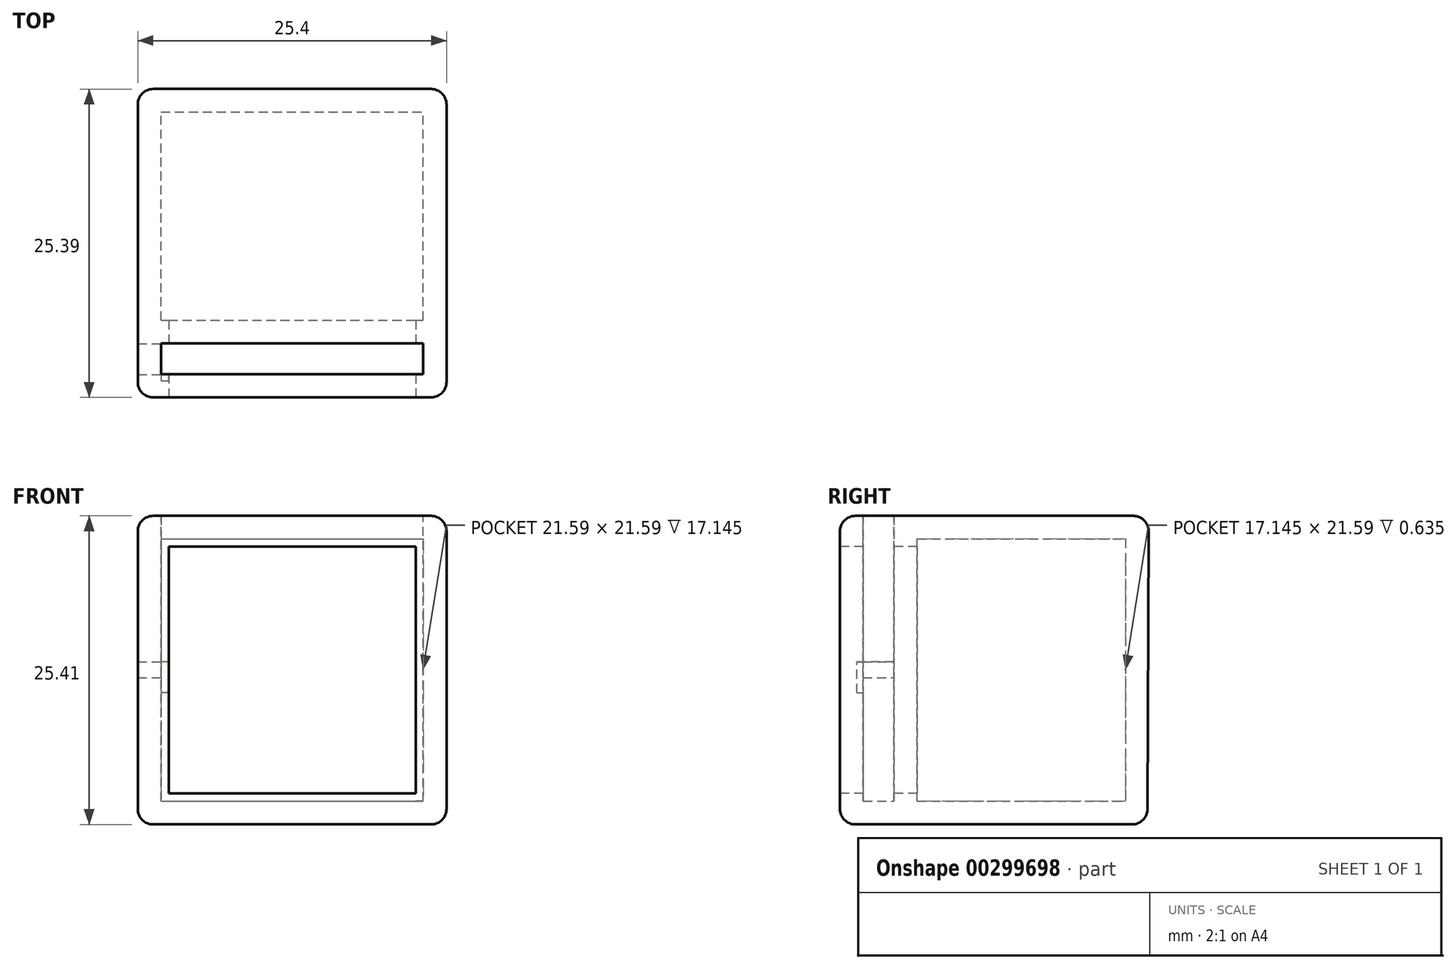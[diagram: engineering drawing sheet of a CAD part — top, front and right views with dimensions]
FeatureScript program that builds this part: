
annotation { "Feature Type Name" : "Feature", "Feature Type Description" : "" }
export const myFeature = defineFeature(function(context is Context, id is Id, definition is map)
    precondition{}
    {
        {
            var Q0;
            Q0=qCreatedBy(makeId("Front.planeOp"),FACE);
            var sketch = newSketch(context, id + "F0", { "sketchPlane" : qUnion([Q0])});
            skLineSegment(sketch, "E0.top", {"start": v(-12.7, -1.9) * mm, "end": v(12.7, -1.9) * mm});
            skPoint(sketch, "E0.middle", {"position": v(0, 0) * mm});
            skLineSegment(sketch, "E1", {"start": v(10.8, 21.6) * mm, "end": v(10.8, 0) * mm});
            skLineSegment(sketch, "E2", {"start": v(-10.8, 21.6) * mm, "end": v(-10.8, 0) * mm});
            skLineSegment(sketch, "E3.top", {"start": v(-12.7, 23.5) * mm, "end": v(12.7, 23.5) * mm});
            skLineSegment(sketch, "E4", {"start": v(-10.8, 21.6) * mm, "end": v(10.8, 21.6) * mm});
            skLineSegment(sketch, "E5", {"start": v(-10.8, 0) * mm, "end": v(10.8, 0) * mm});
            skLineSegment(sketch, "E6", {"start": v(-12.7, -1.9) * mm, "end": v(-12.7, 23.5) * mm});
            skLineSegment(sketch, "E7", {"start": v(12.7, -1.9) * mm, "end": v(12.7, 23.5) * mm});
            skSolve(sketch);
        }
        {
            var Q0;
            Q0=qCreatedBy(makeId("Right.planeOp"),FACE);
            var sketch = newSketch(context, id + "F1", { "sketchPlane" : qUnion([Q0])});
            skLineSegment(sketch, "E8.bottom", {"start": v(8.57, 23.5) * mm, "end": v(10.48, 23.5) * mm});
            skLineSegment(sketch, "E8.left", {"start": v(8.57, 23.5) * mm, "end": v(8.57, 23.5) * mm});
            skLineSegment(sketch, "E8.right", {"start": v(10.48, 23.5) * mm, "end": v(10.36, -1.9) * mm});
            skLineSegment(sketch, "E9", {"start": v(8.57, -1.9) * mm, "end": v(10.36, -1.9) * mm});
            skLineSegment(sketch, "E10.bottom", {"start": v(-8.57, 0.63) * mm, "end": v(-10.48, 0.63) * mm});
            skLineSegment(sketch, "E10.left", {"start": v(-8.57, 0.63) * mm, "end": v(-8.57, -1.9) * mm});
            skLineSegment(sketch, "E11.right", {"start": v(-14.92, 0.63) * mm, "end": v(-14.92, -1.9) * mm});
            skLineSegment(sketch, "E12", {"start": v(-14.92, 20.96) * mm, "end": v(-14.92, 23.5) * mm});
            skLineSegment(sketch, "E13", {"start": v(-8.57, 23.5) * mm, "end": v(-8.57, 20.96) * mm});
            skLineSegment(sketch, "E14", {"start": v(-8.57, 20.96) * mm, "end": v(-10.48, 20.95) * mm});
            skLineSegment(sketch, "E15", {"start": v(-10.48, 20.95) * mm, "end": v(-10.48, 23.5) * mm});
            skLineSegment(sketch, "E16", {"start": v(-13.02, 23.5) * mm, "end": v(-13.02, 20.96) * mm});
            skLineSegment(sketch, "E17", {"start": v(-13.02, 20.96) * mm, "end": v(-14.92, 20.96) * mm});
            skLineSegment(sketch, "E18", {"start": v(-13.02, 23.5) * mm, "end": v(-14.92, 23.5) * mm});
            skLineSegment(sketch, "E19", {"start": v(-8.57, 23.5) * mm, "end": v(-10.48, 23.5) * mm});
            skLineSegment(sketch, "E20", {"start": v(-14.92, -1.9) * mm, "end": v(-8.57, -1.9) * mm});
            skLineSegment(sketch, "E21", {"start": v(-10.48, 0.63) * mm, "end": v(-10.48, 0) * mm});
            skLineSegment(sketch, "E22", {"start": v(-10.48, 0) * mm, "end": v(-13.02, 0) * mm});
            skLineSegment(sketch, "E23", {"start": v(-13.02, 0) * mm, "end": v(-13.02, 0.63) * mm});
            skLineSegment(sketch, "E24", {"start": v(-13.02, 0.63) * mm, "end": v(-14.92, 0.63) * mm});
            skLineSegment(sketch, "E25", {"start": v(8.57, -1.9) * mm, "end": v(8.57, 23.5) * mm});
            skSolve(sketch);
        }
        {
            var Q0;
            Q0=makeQuery(id+"F0.imprint","IMPRINT",FACE,{"disambiguationData":[TD([[makeQuery(id+"F0.imprint","IMPRINT",EDGE,{"derivedFrom":sQuery(id+"F0.wireOp",EDGE,"E0.top")}),1.0]])]});
            extrude(context, id + "F2", {"entities" : qUnion([Q0]), "endBound" : BoundingType.SYMMETRIC, "depth" : 17.14 * mm});
        }
        {
            var Q0;
            Q0 = qSketchRegion(id + "F1", true);
            extrude(context, id + "F3", {"entities" : qUnion([Q0]), "endBound" : BoundingType.SYMMETRIC, "depth" : 25.4 * mm});
        }
        {
            var Q0;
            Q0=qCreatedBy(makeId("Top.planeOp"),FACE);
            var sketch = newSketch(context, id + "F4", { "sketchPlane" : qUnion([Q0])});
            skLineSegment(sketch, "E26", {"start": v(-12.7, -8.57) * mm, "end": v(-12.7, -14.92) * mm});
            skLineSegment(sketch, "E27", {"start": v(-12.7, -14.92) * mm, "end": v(-10.16, -14.92) * mm});
            skLineSegment(sketch, "E28", {"start": v(-10.16, -14.92) * mm, "end": v(-10.16, -13.02) * mm});
            skLineSegment(sketch, "E29", {"start": v(-10.16, -13.02) * mm, "end": v(-10.8, -13.02) * mm});
            skLineSegment(sketch, "E30", {"start": v(-10.8, -13.02) * mm, "end": v(-10.8, -10.48) * mm});
            skLineSegment(sketch, "E31", {"start": v(-10.8, -10.48) * mm, "end": v(-10.16, -10.48) * mm});
            skLineSegment(sketch, "E32", {"start": v(-10.16, -10.48) * mm, "end": v(-10.16, -8.57) * mm});
            skLineSegment(sketch, "E33", {"start": v(-10.16, -8.57) * mm, "end": v(-12.7, -8.57) * mm});
            skLineSegment(sketch, "E34.MirrorCS", {"start": v(10.16, -8.57) * mm, "end": v(12.7, -8.57) * mm});
            skLineSegment(sketch, "E35.MirrorCS", {"start": v(10.16, -10.48) * mm, "end": v(10.16, -8.57) * mm});
            skLineSegment(sketch, "E36.MirrorCS", {"start": v(10.8, -10.48) * mm, "end": v(10.16, -10.48) * mm});
            skLineSegment(sketch, "E37.MirrorCS", {"start": v(10.8, -13.02) * mm, "end": v(10.8, -10.48) * mm});
            skLineSegment(sketch, "E38.MirrorCS", {"start": v(10.16, -13.02) * mm, "end": v(10.8, -13.02) * mm});
            skLineSegment(sketch, "E39.MirrorCS", {"start": v(10.16, -14.92) * mm, "end": v(10.16, -13.02) * mm});
            skLineSegment(sketch, "E40.MirrorCS", {"start": v(12.7, -8.57) * mm, "end": v(12.7, -14.92) * mm});
            skLineSegment(sketch, "E41.MirrorCS", {"start": v(12.7, -14.92) * mm, "end": v(10.16, -14.92) * mm});
            skSolve(sketch);
        }
        {
            var Q0;
            Q0=makeQuery(id+"F4.imprint","IMPRINT",FACE,{"disambiguationData":[TD([[makeQuery(id+"F4.imprint","IMPRINT",EDGE,{"derivedFrom":sQuery(id+"F4.wireOp",EDGE,"E26")}),1.0]])]});
            var Q1;
            Q1=makeQuery(id+"F4.imprint","IMPRINT",FACE,{"disambiguationData":[TD([[makeQuery(id+"F4.imprint","IMPRINT",EDGE,{"derivedFrom":sQuery(id+"F4.wireOp",EDGE,"E34.MirrorCS")}),-1.0]])]});
            extrude(context, id + "F5", {"entities" : qUnion([Q0, Q1]), "depth" : 23.5 * mm});
        }
        {
            var Q0;
            Q0=makeQuery(id+"F5.opExtrude","SWEPT_BODY",BODY,{"disambiguationData":[OSD([sQuery(id+"F4.wireOp",EDGE,"E34.MirrorCS"),sQuery(id+"F4.wireOp",EDGE,"E35.MirrorCS"),sQuery(id+"F4.wireOp",EDGE,"E36.MirrorCS"),sQuery(id+"F4.wireOp",EDGE,"E37.MirrorCS"),sQuery(id+"F4.wireOp",EDGE,"E38.MirrorCS"),sQuery(id+"F4.wireOp",EDGE,"E39.MirrorCS"),sQuery(id+"F4.wireOp",EDGE,"E40.MirrorCS"),sQuery(id+"F4.wireOp",EDGE,"E41.MirrorCS")])]});
            var Q1;
            Q1=makeQuery(id+"F5.opExtrude","SWEPT_BODY",BODY,{"disambiguationData":[OSD([sQuery(id+"F4.wireOp",EDGE,"E26"),sQuery(id+"F4.wireOp",EDGE,"E27"),sQuery(id+"F4.wireOp",EDGE,"E28"),sQuery(id+"F4.wireOp",EDGE,"E29"),sQuery(id+"F4.wireOp",EDGE,"E30"),sQuery(id+"F4.wireOp",EDGE,"E31"),sQuery(id+"F4.wireOp",EDGE,"E32"),sQuery(id+"F4.wireOp",EDGE,"E33")])]});
            var Q2;
            Q2=makeQuery(id+"F3.opExtrude","SWEPT_BODY",BODY,{"disambiguationData":[OSD([sQuery(id+"F1.wireOp",EDGE,"E13"),sQuery(id+"F1.wireOp",EDGE,"E14"),sQuery(id+"F1.wireOp",EDGE,"E15"),sQuery(id+"F1.wireOp",EDGE,"E19")])]});
            var Q3;
            Q3=makeQuery(id+"F3.opExtrude","SWEPT_BODY",BODY,{"disambiguationData":[OSD([sQuery(id+"F1.wireOp",EDGE,"E12"),sQuery(id+"F1.wireOp",EDGE,"E16"),sQuery(id+"F1.wireOp",EDGE,"E17"),sQuery(id+"F1.wireOp",EDGE,"E18")])]});
            var Q4;
            Q4=makeQuery(id+"F3.opExtrude","SWEPT_BODY",BODY,{"disambiguationData":[OSD([sQuery(id+"F1.wireOp",EDGE,"E10.bottom"),sQuery(id+"F1.wireOp",EDGE,"E10.left"),sQuery(id+"F1.wireOp",EDGE,"E11.right"),sQuery(id+"F1.wireOp",EDGE,"E20"),sQuery(id+"F1.wireOp",EDGE,"E21"),sQuery(id+"F1.wireOp",EDGE,"E22"),sQuery(id+"F1.wireOp",EDGE,"E23"),sQuery(id+"F1.wireOp",EDGE,"E24")])]});
            var Q5;
            Q5=makeQuery(id+"F3.opExtrude","SWEPT_BODY",BODY,{"disambiguationData":[OSD([sQuery(id+"F1.wireOp",EDGE,"E8.bottom"),sQuery(id+"F1.wireOp",EDGE,"E8.right"),sQuery(id+"F1.wireOp",EDGE,"E9"),sQuery(id+"F1.wireOp",EDGE,"E25")])]});
            var Q6;
            Q6=makeQuery(id+"F2.opExtrude","SWEPT_BODY",BODY,{"disambiguationData":[OSD([sQuery(id+"F0.wireOp",EDGE,"E0.top"),sQuery(id+"F0.wireOp",EDGE,"E1"),sQuery(id+"F0.wireOp",EDGE,"E2"),sQuery(id+"F0.wireOp",EDGE,"E3.top"),sQuery(id+"F0.wireOp",EDGE,"E4"),sQuery(id+"F0.wireOp",EDGE,"E5"),sQuery(id+"F0.wireOp",EDGE,"E6"),sQuery(id+"F0.wireOp",EDGE,"E7")])]});
            booleanBodies(context, id + "F6", {"operationType" : BooleanOperationType.UNION, "tools" : qUnion([Q0, Q1, Q2, Q3, Q4, Q5, Q6])});
        }
        {
            var Q0;
            Q0=qCreatedBy(makeId("Right.planeOp"),FACE);
            var sketch = newSketch(context, id + "F7", { "sketchPlane" : qUnion([Q0])});
            skLineSegment(sketch, "E42.bottom", {"start": v(-10.5, 10.16) * mm, "end": v(-13.03, 10.16) * mm});
            skLineSegment(sketch, "E42.top", {"start": v(-10.5, 11.47) * mm, "end": v(-13.03, 11.47) * mm});
            skLineSegment(sketch, "E42.left", {"start": v(-10.5, 10.16) * mm, "end": v(-10.5, 11.47) * mm});
            skLineSegment(sketch, "E42.right", {"start": v(-13.03, 10.16) * mm, "end": v(-13.03, 11.47) * mm});
            skLineSegment(sketch, "E43", {"start": v(-13.03, 11.47) * mm, "end": v(-13.54, 11.47) * mm});
            skLineSegment(sketch, "E44", {"start": v(-13.54, 11.47) * mm, "end": v(-13.54, 8.93) * mm});
            skLineSegment(sketch, "E45", {"start": v(-12.65, 10.16) * mm, "end": v(-12.65, 8.93) * mm});
            skLineSegment(sketch, "E46", {"start": v(-12.65, 8.93) * mm, "end": v(-13.54, 8.93) * mm});
            skSolve(sketch);
        }
        {
            var Q0;
            Q0=makeQuery(id+"F7.imprint","IMPRINT",FACE,{"disambiguationData":[TD([[makeQuery(id+"F7.imprint","IMPRINT",EDGE,{"derivedFrom":sQuery(id+"F7.wireOp",EDGE,"E42.bottom")}),-1.0]])]});
            extrude(context, id + "F8", {"entities" : qUnion([Q0]), "operationType" : NewBodyOperationType.REMOVE, "oppositeDirection" : true, "depth" : 12.7 * mm});
        }
        {
            var Q0;
            Q0=makeQuery(id+"F7.imprint","IMPRINT",FACE,{"disambiguationData":[TD([[makeQuery(id+"F7.imprint","IMPRINT",EDGE,{"derivedFrom":sQuery(id+"F7.wireOp",EDGE,"E42.right")}),1.0]])]});
            extrude(context, id + "F9", {"entities" : qUnion([Q0]), "operationType" : NewBodyOperationType.REMOVE, "oppositeDirection" : true, "depth" : 10.8 * mm});
        }
        {
            var Q0;
            Q0=makeQuery(id+"F2.opExtrude","SWEPT_EDGE",EDGE,{"disambiguationData":[OSD([sQuery(id+"F0.wireOp",EDGE,"E3.top"),sQuery(id+"F0.wireOp",EDGE,"E7")])]});
            var Q1;
            Q1=makeQuery(id+"F3.opExtrude","CAP_EDGE",EDGE,{"disambiguationData":[OSD([sQuery(id+"F1.wireOp",EDGE,"E8.bottom")])],"isStart":false});
            var Q2;
            {var subQ0=sQuery(id+"F4.wireOp",EDGE,"E40.MirrorCS");Q2=makeQuery(id+"F6.opBoolean","SPLIT",EDGE,{"disambiguationData":[TD([makeQuery(id+"F2.opExtrude","SWEPT_FACE",FACE,{"disambiguationData":[OSD([sQuery(id+"F0.wireOp",EDGE,"E3.top")])]}),makeQuery(id+"F2.opExtrude","SWEPT_FACE",FACE,{"disambiguationData":[OSD([sQuery(id+"F0.wireOp",EDGE,"E7")])]}),makeQuery(id+"F3.opExtrude","CAP_FACE",FACE,{"disambiguationData":[OSD([sQuery(id+"F1.wireOp",EDGE,"E8.bottom"),sQuery(id+"F1.wireOp",EDGE,"E8.right"),sQuery(id+"F1.wireOp",EDGE,"E9"),sQuery(id+"F1.wireOp",EDGE,"E25")])],"isStart":false}),makeQuery(id+"F3.opExtrude","CAP_FACE",FACE,{"disambiguationData":[OSD([sQuery(id+"F1.wireOp",EDGE,"E10.bottom"),sQuery(id+"F1.wireOp",EDGE,"E10.left"),sQuery(id+"F1.wireOp",EDGE,"E11.right"),sQuery(id+"F1.wireOp",EDGE,"E20"),sQuery(id+"F1.wireOp",EDGE,"E21"),sQuery(id+"F1.wireOp",EDGE,"E22"),sQuery(id+"F1.wireOp",EDGE,"E23"),sQuery(id+"F1.wireOp",EDGE,"E24")])],"isStart":false}),makeQuery(id+"F3.opExtrude","CAP_FACE",FACE,{"disambiguationData":[OSD([sQuery(id+"F1.wireOp",EDGE,"E13"),sQuery(id+"F1.wireOp",EDGE,"E14"),sQuery(id+"F1.wireOp",EDGE,"E15"),sQuery(id+"F1.wireOp",EDGE,"E19")])],"isStart":false}),makeQuery(id+"F3.opExtrude","SWEPT_FACE",FACE,{"disambiguationData":[OSD([sQuery(id+"F1.wireOp",EDGE,"E18")])]}),makeQuery(id+"F5.opExtrude","CAP_FACE",FACE,{"disambiguationData":[OSD([sQuery(id+"F4.wireOp",EDGE,"E26"),sQuery(id+"F4.wireOp",EDGE,"E27"),sQuery(id+"F4.wireOp",EDGE,"E28"),sQuery(id+"F4.wireOp",EDGE,"E29"),sQuery(id+"F4.wireOp",EDGE,"E30"),sQuery(id+"F4.wireOp",EDGE,"E31"),sQuery(id+"F4.wireOp",EDGE,"E32"),sQuery(id+"F4.wireOp",EDGE,"E33")])],"isStart":false}),makeQuery(id+"F5.opExtrude","CAP_FACE",FACE,{"disambiguationData":[OSD([sQuery(id+"F4.wireOp",EDGE,"E34.MirrorCS"),sQuery(id+"F4.wireOp",EDGE,"E35.MirrorCS"),sQuery(id+"F4.wireOp",EDGE,"E36.MirrorCS"),sQuery(id+"F4.wireOp",EDGE,"E37.MirrorCS"),sQuery(id+"F4.wireOp",EDGE,"E38.MirrorCS"),sQuery(id+"F4.wireOp",EDGE,"E39.MirrorCS"),subQ0,sQuery(id+"F4.wireOp",EDGE,"E41.MirrorCS")])],"isStart":false}),makeQuery(id+"F5.opExtrude","SWEPT_FACE",FACE,{"disambiguationData":[OSD([subQ0])]})])],"derivedFrom":makeQuery(id+"F5.opExtrude","CAP_EDGE",EDGE,{"disambiguationData":[OSD([subQ0])],"isStart":false})});}
            var Q3;
            {var subQ0=sQuery(id+"F4.wireOp",EDGE,"E41.MirrorCS");var subQ1=sQuery(id+"F4.wireOp",EDGE,"E40.MirrorCS");Q3=makeQuery(id+"F6.opBoolean","SPLIT",EDGE,{"disambiguationData":[TD([makeQuery(id+"F2.opExtrude","SWEPT_FACE",FACE,{"disambiguationData":[OSD([sQuery(id+"F0.wireOp",EDGE,"E7")])]}),makeQuery(id+"F3.opExtrude","CAP_FACE",FACE,{"disambiguationData":[OSD([sQuery(id+"F1.wireOp",EDGE,"E8.bottom"),sQuery(id+"F1.wireOp",EDGE,"E8.right"),sQuery(id+"F1.wireOp",EDGE,"E9"),sQuery(id+"F1.wireOp",EDGE,"E25")])],"isStart":false}),makeQuery(id+"F3.opExtrude","CAP_FACE",FACE,{"disambiguationData":[OSD([sQuery(id+"F1.wireOp",EDGE,"E10.bottom"),sQuery(id+"F1.wireOp",EDGE,"E10.left"),sQuery(id+"F1.wireOp",EDGE,"E11.right"),sQuery(id+"F1.wireOp",EDGE,"E20"),sQuery(id+"F1.wireOp",EDGE,"E21"),sQuery(id+"F1.wireOp",EDGE,"E22"),sQuery(id+"F1.wireOp",EDGE,"E23"),sQuery(id+"F1.wireOp",EDGE,"E24")])],"isStart":false}),makeQuery(id+"F3.opExtrude","CAP_FACE",FACE,{"disambiguationData":[OSD([sQuery(id+"F1.wireOp",EDGE,"E13"),sQuery(id+"F1.wireOp",EDGE,"E14"),sQuery(id+"F1.wireOp",EDGE,"E15"),sQuery(id+"F1.wireOp",EDGE,"E19")])],"isStart":false}),makeQuery(id+"F3.opExtrude","SWEPT_FACE",FACE,{"disambiguationData":[OSD([sQuery(id+"F1.wireOp",EDGE,"E18")])]}),makeQuery(id+"F5.opExtrude","CAP_FACE",FACE,{"disambiguationData":[OSD([sQuery(id+"F4.wireOp",EDGE,"E26"),sQuery(id+"F4.wireOp",EDGE,"E27"),sQuery(id+"F4.wireOp",EDGE,"E28"),sQuery(id+"F4.wireOp",EDGE,"E29"),sQuery(id+"F4.wireOp",EDGE,"E30"),sQuery(id+"F4.wireOp",EDGE,"E31"),sQuery(id+"F4.wireOp",EDGE,"E32"),sQuery(id+"F4.wireOp",EDGE,"E33")])],"isStart":false}),makeQuery(id+"F5.opExtrude","CAP_FACE",FACE,{"disambiguationData":[OSD([sQuery(id+"F4.wireOp",EDGE,"E34.MirrorCS"),sQuery(id+"F4.wireOp",EDGE,"E35.MirrorCS"),sQuery(id+"F4.wireOp",EDGE,"E36.MirrorCS"),sQuery(id+"F4.wireOp",EDGE,"E37.MirrorCS"),sQuery(id+"F4.wireOp",EDGE,"E38.MirrorCS"),sQuery(id+"F4.wireOp",EDGE,"E39.MirrorCS"),subQ1,subQ0])],"isStart":false}),makeQuery(id+"F5.opExtrude","SWEPT_FACE",FACE,{"disambiguationData":[OSD([subQ1])]}),makeQuery(id+"F5.opExtrude","SWEPT_FACE",FACE,{"disambiguationData":[OSD([subQ0])]})])],"derivedFrom":makeQuery(id+"F5.opExtrude","CAP_EDGE",EDGE,{"disambiguationData":[OSD([subQ1])],"isStart":false})});}
            var Q4;
            {var subQ0=sQuery(id+"F4.wireOp",EDGE,"E40.MirrorCS");Q4=makeQuery(id+"F6.opBoolean","SPLIT",EDGE,{"disambiguationData":[TD([makeQuery(id+"F2.opExtrude","SWEPT_FACE",FACE,{"disambiguationData":[OSD([sQuery(id+"F0.wireOp",EDGE,"E7")])]}),makeQuery(id+"F3.opExtrude","CAP_FACE",FACE,{"disambiguationData":[OSD([sQuery(id+"F1.wireOp",EDGE,"E8.bottom"),sQuery(id+"F1.wireOp",EDGE,"E8.right"),sQuery(id+"F1.wireOp",EDGE,"E9"),sQuery(id+"F1.wireOp",EDGE,"E25")])],"isStart":false}),makeQuery(id+"F3.opExtrude","CAP_FACE",FACE,{"disambiguationData":[OSD([sQuery(id+"F1.wireOp",EDGE,"E10.bottom"),sQuery(id+"F1.wireOp",EDGE,"E10.left"),sQuery(id+"F1.wireOp",EDGE,"E11.right"),sQuery(id+"F1.wireOp",EDGE,"E20"),sQuery(id+"F1.wireOp",EDGE,"E21"),sQuery(id+"F1.wireOp",EDGE,"E22"),sQuery(id+"F1.wireOp",EDGE,"E23"),sQuery(id+"F1.wireOp",EDGE,"E24")])],"isStart":false}),makeQuery(id+"F3.opExtrude","CAP_FACE",FACE,{"disambiguationData":[OSD([sQuery(id+"F1.wireOp",EDGE,"E13"),sQuery(id+"F1.wireOp",EDGE,"E14"),sQuery(id+"F1.wireOp",EDGE,"E15"),sQuery(id+"F1.wireOp",EDGE,"E19")])],"isStart":false}),makeQuery(id+"F3.opExtrude","SWEPT_FACE",FACE,{"disambiguationData":[OSD([sQuery(id+"F1.wireOp",EDGE,"E18")])]}),makeQuery(id+"F5.opExtrude","CAP_FACE",FACE,{"disambiguationData":[OSD([sQuery(id+"F4.wireOp",EDGE,"E26"),sQuery(id+"F4.wireOp",EDGE,"E27"),sQuery(id+"F4.wireOp",EDGE,"E28"),sQuery(id+"F4.wireOp",EDGE,"E29"),sQuery(id+"F4.wireOp",EDGE,"E30"),sQuery(id+"F4.wireOp",EDGE,"E31"),sQuery(id+"F4.wireOp",EDGE,"E32"),sQuery(id+"F4.wireOp",EDGE,"E33")])],"isStart":false}),makeQuery(id+"F5.opExtrude","CAP_FACE",FACE,{"disambiguationData":[OSD([sQuery(id+"F4.wireOp",EDGE,"E34.MirrorCS"),sQuery(id+"F4.wireOp",EDGE,"E35.MirrorCS"),sQuery(id+"F4.wireOp",EDGE,"E36.MirrorCS"),sQuery(id+"F4.wireOp",EDGE,"E37.MirrorCS"),sQuery(id+"F4.wireOp",EDGE,"E38.MirrorCS"),sQuery(id+"F4.wireOp",EDGE,"E39.MirrorCS"),subQ0,sQuery(id+"F4.wireOp",EDGE,"E41.MirrorCS")])],"isStart":false}),makeQuery(id+"F5.opExtrude","SWEPT_FACE",FACE,{"disambiguationData":[OSD([subQ0])]})])],"derivedFrom":makeQuery(id+"F5.opExtrude","CAP_EDGE",EDGE,{"disambiguationData":[OSD([subQ0])],"isStart":false})});}
            var Q5;
            {var subQ0=sQuery(id+"F4.wireOp",EDGE,"E41.MirrorCS");var subQ1=sQuery(id+"F4.wireOp",EDGE,"E40.MirrorCS");Q5=makeQuery(id+"F6.opBoolean","SPLIT",EDGE,{"disambiguationData":[TD([makeQuery(id+"F2.opExtrude","SWEPT_FACE",FACE,{"disambiguationData":[OSD([sQuery(id+"F0.wireOp",EDGE,"E7")])]}),makeQuery(id+"F3.opExtrude","CAP_FACE",FACE,{"disambiguationData":[OSD([sQuery(id+"F1.wireOp",EDGE,"E8.bottom"),sQuery(id+"F1.wireOp",EDGE,"E8.right"),sQuery(id+"F1.wireOp",EDGE,"E9"),sQuery(id+"F1.wireOp",EDGE,"E25")])],"isStart":false}),makeQuery(id+"F3.opExtrude","CAP_FACE",FACE,{"disambiguationData":[OSD([sQuery(id+"F1.wireOp",EDGE,"E10.bottom"),sQuery(id+"F1.wireOp",EDGE,"E10.left"),sQuery(id+"F1.wireOp",EDGE,"E11.right"),sQuery(id+"F1.wireOp",EDGE,"E20"),sQuery(id+"F1.wireOp",EDGE,"E21"),sQuery(id+"F1.wireOp",EDGE,"E22"),sQuery(id+"F1.wireOp",EDGE,"E23"),sQuery(id+"F1.wireOp",EDGE,"E24")])],"isStart":false}),makeQuery(id+"F3.opExtrude","CAP_FACE",FACE,{"disambiguationData":[OSD([sQuery(id+"F1.wireOp",EDGE,"E13"),sQuery(id+"F1.wireOp",EDGE,"E14"),sQuery(id+"F1.wireOp",EDGE,"E15"),sQuery(id+"F1.wireOp",EDGE,"E19")])],"isStart":false}),makeQuery(id+"F5.opExtrude","SWEPT_FACE",FACE,{"disambiguationData":[OSD([subQ1])]}),makeQuery(id+"F5.opExtrude","SWEPT_FACE",FACE,{"disambiguationData":[OSD([subQ0])]})])],"derivedFrom":makeQuery(id+"F5.opExtrude","SWEPT_EDGE",EDGE,{"disambiguationData":[OSD([subQ1,subQ0])]})});}
            var Q6;
            Q6=makeQuery(id+"F3.opExtrude","SWEPT_EDGE",EDGE,{"disambiguationData":[OSD([sQuery(id+"F1.wireOp",EDGE,"E12"),sQuery(id+"F1.wireOp",EDGE,"E18")])]});
            var Q7;
            Q7=makeQuery(id+"F2.opExtrude","SWEPT_EDGE",EDGE,{"disambiguationData":[OSD([sQuery(id+"F0.wireOp",EDGE,"E0.top"),sQuery(id+"F0.wireOp",EDGE,"E7")])]});
            var Q8;
            Q8=makeQuery(id+"F3.opExtrude","SWEPT_EDGE",EDGE,{"disambiguationData":[OSD([sQuery(id+"F1.wireOp",EDGE,"E11.right"),sQuery(id+"F1.wireOp",EDGE,"E20")])]});
            var Q9;
            {var subQ0=sQuery(id+"F1.wireOp",EDGE,"E11.right");var subQ1=sQuery(id+"F4.wireOp",EDGE,"E41.MirrorCS");var subQ2=sQuery(id+"F4.wireOp",EDGE,"E40.MirrorCS");Q9=makeQuery(id+"F6.opBoolean","SPLIT",EDGE,{"disambiguationData":[TD([makeQuery(id+"F2.opExtrude","SWEPT_FACE",FACE,{"disambiguationData":[OSD([sQuery(id+"F0.wireOp",EDGE,"E7")])]}),makeQuery(id+"F3.opExtrude","CAP_FACE",FACE,{"disambiguationData":[OSD([sQuery(id+"F1.wireOp",EDGE,"E8.bottom"),sQuery(id+"F1.wireOp",EDGE,"E8.right"),sQuery(id+"F1.wireOp",EDGE,"E9"),sQuery(id+"F1.wireOp",EDGE,"E25")])],"isStart":false}),makeQuery(id+"F3.opExtrude","CAP_FACE",FACE,{"disambiguationData":[OSD([sQuery(id+"F1.wireOp",EDGE,"E10.bottom"),sQuery(id+"F1.wireOp",EDGE,"E10.left"),subQ0,sQuery(id+"F1.wireOp",EDGE,"E20"),sQuery(id+"F1.wireOp",EDGE,"E21"),sQuery(id+"F1.wireOp",EDGE,"E22"),sQuery(id+"F1.wireOp",EDGE,"E23"),sQuery(id+"F1.wireOp",EDGE,"E24")])],"isStart":false}),makeQuery(id+"F3.opExtrude","SWEPT_FACE",FACE,{"disambiguationData":[OSD([subQ0])]}),makeQuery(id+"F3.opExtrude","CAP_FACE",FACE,{"disambiguationData":[OSD([sQuery(id+"F1.wireOp",EDGE,"E13"),sQuery(id+"F1.wireOp",EDGE,"E14"),sQuery(id+"F1.wireOp",EDGE,"E15"),sQuery(id+"F1.wireOp",EDGE,"E19")])],"isStart":false}),makeQuery(id+"F5.opExtrude","SWEPT_FACE",FACE,{"disambiguationData":[OSD([subQ2])]}),makeQuery(id+"F5.opExtrude","SWEPT_FACE",FACE,{"disambiguationData":[OSD([subQ1])]})])],"derivedFrom":makeQuery(id+"F5.opExtrude","SWEPT_EDGE",EDGE,{"disambiguationData":[OSD([subQ2,subQ1])]})});}
            var Q10;
            Q10=makeQuery(id+"F3.opExtrude","CAP_EDGE",EDGE,{"disambiguationData":[OSD([sQuery(id+"F1.wireOp",EDGE,"E11.right")])],"isStart":false});
            var Q11;
            {var subQ0=sQuery(id+"F4.wireOp",EDGE,"E26");var subQ1=sQuery(id+"F4.wireOp",EDGE,"E27");Q11=makeQuery(id+"F6.opBoolean","SPLIT",EDGE,{"disambiguationData":[TD([makeQuery(id+"F2.opExtrude","SWEPT_FACE",FACE,{"disambiguationData":[OSD([sQuery(id+"F0.wireOp",EDGE,"E6")])]}),makeQuery(id+"F3.opExtrude","CAP_FACE",FACE,{"disambiguationData":[OSD([sQuery(id+"F1.wireOp",EDGE,"E8.bottom"),sQuery(id+"F1.wireOp",EDGE,"E8.right"),sQuery(id+"F1.wireOp",EDGE,"E9"),sQuery(id+"F1.wireOp",EDGE,"E25")])],"isStart":true}),makeQuery(id+"F3.opExtrude","CAP_FACE",FACE,{"disambiguationData":[OSD([sQuery(id+"F1.wireOp",EDGE,"E10.bottom"),sQuery(id+"F1.wireOp",EDGE,"E10.left"),sQuery(id+"F1.wireOp",EDGE,"E11.right"),sQuery(id+"F1.wireOp",EDGE,"E20"),sQuery(id+"F1.wireOp",EDGE,"E21"),sQuery(id+"F1.wireOp",EDGE,"E22"),sQuery(id+"F1.wireOp",EDGE,"E23"),sQuery(id+"F1.wireOp",EDGE,"E24")])],"isStart":true}),makeQuery(id+"F3.opExtrude","CAP_FACE",FACE,{"disambiguationData":[OSD([sQuery(id+"F1.wireOp",EDGE,"E13"),sQuery(id+"F1.wireOp",EDGE,"E14"),sQuery(id+"F1.wireOp",EDGE,"E15"),sQuery(id+"F1.wireOp",EDGE,"E19")])],"isStart":true}),makeQuery(id+"F5.opExtrude","SWEPT_FACE",FACE,{"disambiguationData":[OSD([subQ0])]}),makeQuery(id+"F5.opExtrude","SWEPT_FACE",FACE,{"disambiguationData":[OSD([subQ1])]})])],"derivedFrom":makeQuery(id+"F5.opExtrude","SWEPT_EDGE",EDGE,{"disambiguationData":[OSD([subQ0,subQ1])]})});}
            var Q12;
            Q12=makeQuery(id+"F3.opExtrude","CAP_EDGE",EDGE,{"disambiguationData":[OSD([sQuery(id+"F1.wireOp",EDGE,"E8.right")])],"isStart":false});
            var Q13;
            Q13=makeQuery(id+"F3.opExtrude","SWEPT_FACE",FACE,{"disambiguationData":[OSD([sQuery(id+"F1.wireOp",EDGE,"E8.right")])]});
            var Q14;
            Q14=makeQuery(id+"F2.opExtrude","SWEPT_EDGE",EDGE,{"disambiguationData":[OSD([sQuery(id+"F0.wireOp",EDGE,"E3.top"),sQuery(id+"F0.wireOp",EDGE,"E6")])]});
            var Q15;
            Q15=makeQuery(id+"F3.opExtrude","CAP_EDGE",EDGE,{"disambiguationData":[OSD([sQuery(id+"F1.wireOp",EDGE,"E8.bottom")])],"isStart":true});
            var Q16;
            {var subQ0=sQuery(id+"F4.wireOp",EDGE,"E26");Q16=makeQuery(id+"F6.opBoolean","SPLIT",EDGE,{"disambiguationData":[TD([makeQuery(id+"F2.opExtrude","SWEPT_FACE",FACE,{"disambiguationData":[OSD([sQuery(id+"F0.wireOp",EDGE,"E3.top")])]}),makeQuery(id+"F2.opExtrude","SWEPT_FACE",FACE,{"disambiguationData":[OSD([sQuery(id+"F0.wireOp",EDGE,"E6")])]}),makeQuery(id+"F3.opExtrude","CAP_FACE",FACE,{"disambiguationData":[OSD([sQuery(id+"F1.wireOp",EDGE,"E8.bottom"),sQuery(id+"F1.wireOp",EDGE,"E8.right"),sQuery(id+"F1.wireOp",EDGE,"E9"),sQuery(id+"F1.wireOp",EDGE,"E25")])],"isStart":true}),makeQuery(id+"F3.opExtrude","CAP_FACE",FACE,{"disambiguationData":[OSD([sQuery(id+"F1.wireOp",EDGE,"E10.bottom"),sQuery(id+"F1.wireOp",EDGE,"E10.left"),sQuery(id+"F1.wireOp",EDGE,"E11.right"),sQuery(id+"F1.wireOp",EDGE,"E20"),sQuery(id+"F1.wireOp",EDGE,"E21"),sQuery(id+"F1.wireOp",EDGE,"E22"),sQuery(id+"F1.wireOp",EDGE,"E23"),sQuery(id+"F1.wireOp",EDGE,"E24")])],"isStart":true}),makeQuery(id+"F3.opExtrude","CAP_FACE",FACE,{"disambiguationData":[OSD([sQuery(id+"F1.wireOp",EDGE,"E13"),sQuery(id+"F1.wireOp",EDGE,"E14"),sQuery(id+"F1.wireOp",EDGE,"E15"),sQuery(id+"F1.wireOp",EDGE,"E19")])],"isStart":true}),makeQuery(id+"F3.opExtrude","SWEPT_FACE",FACE,{"disambiguationData":[OSD([sQuery(id+"F1.wireOp",EDGE,"E18")])]}),makeQuery(id+"F5.opExtrude","SWEPT_FACE",FACE,{"disambiguationData":[OSD([subQ0])]}),makeQuery(id+"F5.opExtrude","CAP_FACE",FACE,{"disambiguationData":[OSD([subQ0,sQuery(id+"F4.wireOp",EDGE,"E27"),sQuery(id+"F4.wireOp",EDGE,"E28"),sQuery(id+"F4.wireOp",EDGE,"E29"),sQuery(id+"F4.wireOp",EDGE,"E30"),sQuery(id+"F4.wireOp",EDGE,"E31"),sQuery(id+"F4.wireOp",EDGE,"E32"),sQuery(id+"F4.wireOp",EDGE,"E33")])],"isStart":false}),makeQuery(id+"F5.opExtrude","CAP_FACE",FACE,{"disambiguationData":[OSD([sQuery(id+"F4.wireOp",EDGE,"E34.MirrorCS"),sQuery(id+"F4.wireOp",EDGE,"E35.MirrorCS"),sQuery(id+"F4.wireOp",EDGE,"E36.MirrorCS"),sQuery(id+"F4.wireOp",EDGE,"E37.MirrorCS"),sQuery(id+"F4.wireOp",EDGE,"E38.MirrorCS"),sQuery(id+"F4.wireOp",EDGE,"E39.MirrorCS"),sQuery(id+"F4.wireOp",EDGE,"E40.MirrorCS"),sQuery(id+"F4.wireOp",EDGE,"E41.MirrorCS")])],"isStart":false})])],"derivedFrom":makeQuery(id+"F5.opExtrude","CAP_EDGE",EDGE,{"disambiguationData":[OSD([subQ0])],"isStart":false})});}
            var Q17;
            {var subQ0=sQuery(id+"F4.wireOp",EDGE,"E26");Q17=makeQuery(id+"F6.opBoolean","SPLIT",EDGE,{"disambiguationData":[TD([makeQuery(id+"F2.opExtrude","SWEPT_FACE",FACE,{"disambiguationData":[OSD([sQuery(id+"F0.wireOp",EDGE,"E6")])]}),makeQuery(id+"F3.opExtrude","CAP_FACE",FACE,{"disambiguationData":[OSD([sQuery(id+"F1.wireOp",EDGE,"E8.bottom"),sQuery(id+"F1.wireOp",EDGE,"E8.right"),sQuery(id+"F1.wireOp",EDGE,"E9"),sQuery(id+"F1.wireOp",EDGE,"E25")])],"isStart":true}),makeQuery(id+"F3.opExtrude","CAP_FACE",FACE,{"disambiguationData":[OSD([sQuery(id+"F1.wireOp",EDGE,"E10.bottom"),sQuery(id+"F1.wireOp",EDGE,"E10.left"),sQuery(id+"F1.wireOp",EDGE,"E11.right"),sQuery(id+"F1.wireOp",EDGE,"E20"),sQuery(id+"F1.wireOp",EDGE,"E21"),sQuery(id+"F1.wireOp",EDGE,"E22"),sQuery(id+"F1.wireOp",EDGE,"E23"),sQuery(id+"F1.wireOp",EDGE,"E24")])],"isStart":true}),makeQuery(id+"F3.opExtrude","CAP_FACE",FACE,{"disambiguationData":[OSD([sQuery(id+"F1.wireOp",EDGE,"E13"),sQuery(id+"F1.wireOp",EDGE,"E14"),sQuery(id+"F1.wireOp",EDGE,"E15"),sQuery(id+"F1.wireOp",EDGE,"E19")])],"isStart":true}),makeQuery(id+"F3.opExtrude","SWEPT_FACE",FACE,{"disambiguationData":[OSD([sQuery(id+"F1.wireOp",EDGE,"E18")])]}),makeQuery(id+"F5.opExtrude","SWEPT_FACE",FACE,{"disambiguationData":[OSD([subQ0])]}),makeQuery(id+"F5.opExtrude","CAP_FACE",FACE,{"disambiguationData":[OSD([subQ0,sQuery(id+"F4.wireOp",EDGE,"E27"),sQuery(id+"F4.wireOp",EDGE,"E28"),sQuery(id+"F4.wireOp",EDGE,"E29"),sQuery(id+"F4.wireOp",EDGE,"E30"),sQuery(id+"F4.wireOp",EDGE,"E31"),sQuery(id+"F4.wireOp",EDGE,"E32"),sQuery(id+"F4.wireOp",EDGE,"E33")])],"isStart":false}),makeQuery(id+"F5.opExtrude","CAP_FACE",FACE,{"disambiguationData":[OSD([sQuery(id+"F4.wireOp",EDGE,"E34.MirrorCS"),sQuery(id+"F4.wireOp",EDGE,"E35.MirrorCS"),sQuery(id+"F4.wireOp",EDGE,"E36.MirrorCS"),sQuery(id+"F4.wireOp",EDGE,"E37.MirrorCS"),sQuery(id+"F4.wireOp",EDGE,"E38.MirrorCS"),sQuery(id+"F4.wireOp",EDGE,"E39.MirrorCS"),sQuery(id+"F4.wireOp",EDGE,"E40.MirrorCS"),sQuery(id+"F4.wireOp",EDGE,"E41.MirrorCS")])],"isStart":false})])],"derivedFrom":makeQuery(id+"F5.opExtrude","CAP_EDGE",EDGE,{"disambiguationData":[OSD([subQ0])],"isStart":false})});}
            var Q18;
            {var subQ0=sQuery(id+"F4.wireOp",EDGE,"E26");var subQ1=sQuery(id+"F4.wireOp",EDGE,"E27");Q18=makeQuery(id+"F6.opBoolean","SPLIT",EDGE,{"disambiguationData":[TD([makeQuery(id+"F2.opExtrude","SWEPT_FACE",FACE,{"disambiguationData":[OSD([sQuery(id+"F0.wireOp",EDGE,"E6")])]}),makeQuery(id+"F3.opExtrude","CAP_FACE",FACE,{"disambiguationData":[OSD([sQuery(id+"F1.wireOp",EDGE,"E8.bottom"),sQuery(id+"F1.wireOp",EDGE,"E8.right"),sQuery(id+"F1.wireOp",EDGE,"E9"),sQuery(id+"F1.wireOp",EDGE,"E25")])],"isStart":true}),makeQuery(id+"F3.opExtrude","CAP_FACE",FACE,{"disambiguationData":[OSD([sQuery(id+"F1.wireOp",EDGE,"E10.bottom"),sQuery(id+"F1.wireOp",EDGE,"E10.left"),sQuery(id+"F1.wireOp",EDGE,"E11.right"),sQuery(id+"F1.wireOp",EDGE,"E20"),sQuery(id+"F1.wireOp",EDGE,"E21"),sQuery(id+"F1.wireOp",EDGE,"E22"),sQuery(id+"F1.wireOp",EDGE,"E23"),sQuery(id+"F1.wireOp",EDGE,"E24")])],"isStart":true}),makeQuery(id+"F3.opExtrude","CAP_FACE",FACE,{"disambiguationData":[OSD([sQuery(id+"F1.wireOp",EDGE,"E13"),sQuery(id+"F1.wireOp",EDGE,"E14"),sQuery(id+"F1.wireOp",EDGE,"E15"),sQuery(id+"F1.wireOp",EDGE,"E19")])],"isStart":true}),makeQuery(id+"F3.opExtrude","SWEPT_FACE",FACE,{"disambiguationData":[OSD([sQuery(id+"F1.wireOp",EDGE,"E18")])]}),makeQuery(id+"F5.opExtrude","SWEPT_FACE",FACE,{"disambiguationData":[OSD([subQ0])]}),makeQuery(id+"F5.opExtrude","CAP_FACE",FACE,{"disambiguationData":[OSD([subQ0,subQ1,sQuery(id+"F4.wireOp",EDGE,"E28"),sQuery(id+"F4.wireOp",EDGE,"E29"),sQuery(id+"F4.wireOp",EDGE,"E30"),sQuery(id+"F4.wireOp",EDGE,"E31"),sQuery(id+"F4.wireOp",EDGE,"E32"),sQuery(id+"F4.wireOp",EDGE,"E33")])],"isStart":false}),makeQuery(id+"F5.opExtrude","SWEPT_FACE",FACE,{"disambiguationData":[OSD([subQ1])]}),makeQuery(id+"F5.opExtrude","CAP_FACE",FACE,{"disambiguationData":[OSD([sQuery(id+"F4.wireOp",EDGE,"E34.MirrorCS"),sQuery(id+"F4.wireOp",EDGE,"E35.MirrorCS"),sQuery(id+"F4.wireOp",EDGE,"E36.MirrorCS"),sQuery(id+"F4.wireOp",EDGE,"E37.MirrorCS"),sQuery(id+"F4.wireOp",EDGE,"E38.MirrorCS"),sQuery(id+"F4.wireOp",EDGE,"E39.MirrorCS"),sQuery(id+"F4.wireOp",EDGE,"E40.MirrorCS"),sQuery(id+"F4.wireOp",EDGE,"E41.MirrorCS")])],"isStart":false})])],"derivedFrom":makeQuery(id+"F5.opExtrude","CAP_EDGE",EDGE,{"disambiguationData":[OSD([subQ0])],"isStart":false})});}
            var Q19;
            {var subQ0=sQuery(id+"F4.wireOp",EDGE,"E26");var subQ1=sQuery(id+"F4.wireOp",EDGE,"E27");Q19=makeQuery(id+"F6.opBoolean","SPLIT",EDGE,{"disambiguationData":[TD([makeQuery(id+"F2.opExtrude","SWEPT_FACE",FACE,{"disambiguationData":[OSD([sQuery(id+"F0.wireOp",EDGE,"E6")])]}),makeQuery(id+"F3.opExtrude","CAP_FACE",FACE,{"disambiguationData":[OSD([sQuery(id+"F1.wireOp",EDGE,"E8.bottom"),sQuery(id+"F1.wireOp",EDGE,"E8.right"),sQuery(id+"F1.wireOp",EDGE,"E9"),sQuery(id+"F1.wireOp",EDGE,"E25")])],"isStart":true}),makeQuery(id+"F3.opExtrude","CAP_FACE",FACE,{"disambiguationData":[OSD([sQuery(id+"F1.wireOp",EDGE,"E10.bottom"),sQuery(id+"F1.wireOp",EDGE,"E10.left"),sQuery(id+"F1.wireOp",EDGE,"E11.right"),sQuery(id+"F1.wireOp",EDGE,"E20"),sQuery(id+"F1.wireOp",EDGE,"E21"),sQuery(id+"F1.wireOp",EDGE,"E22"),sQuery(id+"F1.wireOp",EDGE,"E23"),sQuery(id+"F1.wireOp",EDGE,"E24")])],"isStart":true}),makeQuery(id+"F3.opExtrude","CAP_FACE",FACE,{"disambiguationData":[OSD([sQuery(id+"F1.wireOp",EDGE,"E13"),sQuery(id+"F1.wireOp",EDGE,"E14"),sQuery(id+"F1.wireOp",EDGE,"E15"),sQuery(id+"F1.wireOp",EDGE,"E19")])],"isStart":true}),makeQuery(id+"F3.opExtrude","SWEPT_FACE",FACE,{"disambiguationData":[OSD([sQuery(id+"F1.wireOp",EDGE,"E18")])]}),makeQuery(id+"F5.opExtrude","SWEPT_FACE",FACE,{"disambiguationData":[OSD([subQ0])]}),makeQuery(id+"F5.opExtrude","CAP_FACE",FACE,{"disambiguationData":[OSD([subQ0,subQ1,sQuery(id+"F4.wireOp",EDGE,"E28"),sQuery(id+"F4.wireOp",EDGE,"E29"),sQuery(id+"F4.wireOp",EDGE,"E30"),sQuery(id+"F4.wireOp",EDGE,"E31"),sQuery(id+"F4.wireOp",EDGE,"E32"),sQuery(id+"F4.wireOp",EDGE,"E33")])],"isStart":false}),makeQuery(id+"F5.opExtrude","SWEPT_FACE",FACE,{"disambiguationData":[OSD([subQ1])]}),makeQuery(id+"F5.opExtrude","CAP_FACE",FACE,{"disambiguationData":[OSD([sQuery(id+"F4.wireOp",EDGE,"E34.MirrorCS"),sQuery(id+"F4.wireOp",EDGE,"E35.MirrorCS"),sQuery(id+"F4.wireOp",EDGE,"E36.MirrorCS"),sQuery(id+"F4.wireOp",EDGE,"E37.MirrorCS"),sQuery(id+"F4.wireOp",EDGE,"E38.MirrorCS"),sQuery(id+"F4.wireOp",EDGE,"E39.MirrorCS"),sQuery(id+"F4.wireOp",EDGE,"E40.MirrorCS"),sQuery(id+"F4.wireOp",EDGE,"E41.MirrorCS")])],"isStart":false})])],"derivedFrom":makeQuery(id+"F5.opExtrude","SWEPT_EDGE",EDGE,{"disambiguationData":[OSD([subQ0,subQ1])]})});}
            var Q20;
            Q20=makeQuery(id+"F5.opExtrude","CAP_EDGE",EDGE,{"disambiguationData":[OSD([sQuery(id+"F4.wireOp",EDGE,"E27")])],"isStart":false});
            var Q21;
            Q21=makeQuery(id+"F2.opExtrude","SWEPT_EDGE",EDGE,{"disambiguationData":[OSD([sQuery(id+"F0.wireOp",EDGE,"E0.top"),sQuery(id+"F0.wireOp",EDGE,"E6")])]});
            var Q22;
            Q22=makeQuery(id+"F3.opExtrude","CAP_EDGE",EDGE,{"disambiguationData":[OSD([sQuery(id+"F1.wireOp",EDGE,"E20")])],"isStart":true});
            var Q23;
            Q23=makeQuery(id+"F3.opExtrude","CAP_EDGE",EDGE,{"disambiguationData":[OSD([sQuery(id+"F1.wireOp",EDGE,"E9")])],"isStart":true});
            var Q24;
            Q24=makeQuery(id+"F3.opExtrude","CAP_EDGE",EDGE,{"disambiguationData":[OSD([sQuery(id+"F1.wireOp",EDGE,"E11.right")])],"isStart":true});
            fillet(context, id + "F10", {"entities" : qUnion([Q0, Q1, Q2, Q3, Q4, Q5, Q6, Q7, Q8, Q9, Q10, Q11, Q12, Q13, Q14, Q15, Q16, Q17, Q18, Q19, Q20, Q21, Q22, Q23, Q24]), "radius" : 1.27 * mm, "tangentPropagation" : true, "allowEdgeOverflow" : false});
        }
    });
